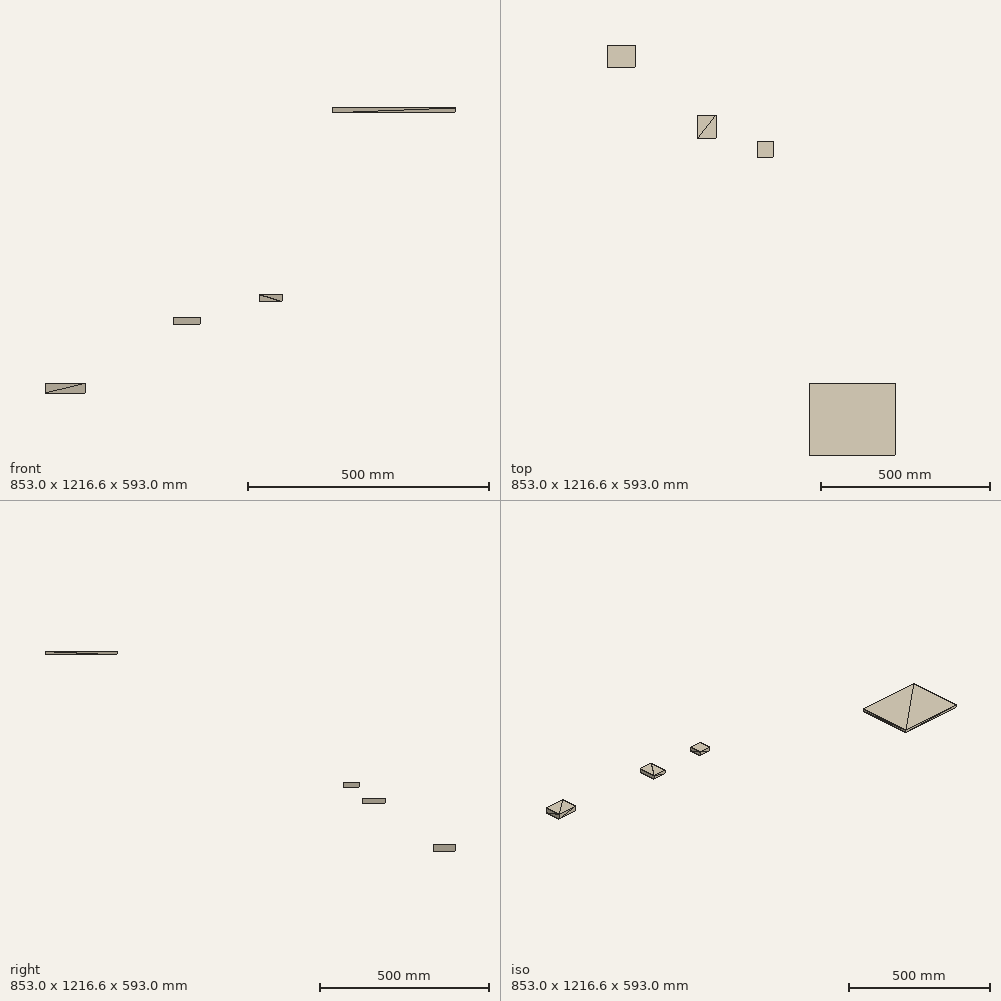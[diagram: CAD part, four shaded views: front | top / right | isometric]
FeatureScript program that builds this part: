
annotation { "Feature Type Name" : "Feature", "Feature Type Description" : "" }
export const myFeature = defineFeature(function(context is Context, id is Id, definition is map)
    precondition{}
    {
        {
            var Q0;
            Q0=qCreatedBy(makeId("Top.planeOp"),FACE);
            var sketch = newSketch(context, id + "F0", { "sketchPlane" : qUnion([Q0])});
            skLineSegment(sketch, "E0.bottom", {"start": v(-671.04, -957.1) * mm, "end": v(-416.04, -957.1) * mm});
            skLineSegment(sketch, "E0.top", {"start": v(-671.04, -1172.1) * mm, "end": v(-416.04, -1172.1) * mm});
            skLineSegment(sketch, "E0.left", {"start": v(-671.04, -957.1) * mm, "end": v(-671.04, -1172.1) * mm});
            skLineSegment(sketch, "E0.right", {"start": v(-416.04, -957.1) * mm, "end": v(-416.04, -1172.1) * mm});
            skSolve(sketch);
        }
        {
            var Q0;
            Q0=qCreatedBy(makeId("Top.planeOp"),FACE);
            var sketch = newSketch(context, id + "F1", { "sketchPlane" : qUnion([Q0])});
            skLineSegment(sketch, "E1.bottom", {"start": v(-508.52, -162.3) * mm, "end": v(-453.52, -162.3) * mm});
            skLineSegment(sketch, "E1.top", {"start": v(-508.52, -232.3) * mm, "end": v(-453.52, -232.3) * mm});
            skLineSegment(sketch, "E1.left", {"start": v(-508.52, -162.3) * mm, "end": v(-508.52, -232.3) * mm});
            skLineSegment(sketch, "E1.right", {"start": v(-453.52, -162.3) * mm, "end": v(-453.52, -232.3) * mm});
            skSolve(sketch);
        }
        {
            var Q0;
            Q0=qCreatedBy(makeId("Top.planeOp"),FACE);
            var sketch = newSketch(context, id + "F2", { "sketchPlane" : qUnion([Q0])});
            skLineSegment(sketch, "E2.bottom", {"start": v(-178.82, -239.95) * mm, "end": v(-130.82, -239.95) * mm});
            skLineSegment(sketch, "E2.top", {"start": v(-178.82, -287.95) * mm, "end": v(-130.82, -287.95) * mm});
            skLineSegment(sketch, "E2.left", {"start": v(-178.82, -239.95) * mm, "end": v(-178.82, -287.95) * mm});
            skLineSegment(sketch, "E2.right", {"start": v(-130.82, -239.95) * mm, "end": v(-130.82, -287.95) * mm});
            skSolve(sketch);
        }
        {
            var Q0;
            Q0=qCreatedBy(makeId("Top.planeOp"),FACE);
            var sketch = newSketch(context, id + "F3", { "sketchPlane" : qUnion([Q0])});
            skLineSegment(sketch, "E3.bottom", {"start": v(-665.08, 44.53) * mm, "end": v(-582.08, 44.53) * mm});
            skLineSegment(sketch, "E3.top", {"start": v(-665.08, -20.47) * mm, "end": v(-582.08, -20.47) * mm});
            skLineSegment(sketch, "E3.left", {"start": v(-665.08, 44.53) * mm, "end": v(-665.08, -20.47) * mm});
            skLineSegment(sketch, "E3.right", {"start": v(-582.08, 44.53) * mm, "end": v(-582.08, -20.47) * mm});
            skSolve(sketch);
        }
        {
            var Q0;
            Q0 = qSketchRegion(id + "F1", true);
            extrude(context, id + "F4", {"entities" : qUnion([Q0]), "depth" : 15 * mm});
        }
        {
            var Q0;
            Q0 = qSketchRegion(id + "F2", true);
            extrude(context, id + "F5", {"entities" : qUnion([Q0]), "depth" : 15 * mm});
        }
        {
            var Q0;
            Q0 = qSketchRegion(id + "F3", true);
            extrude(context, id + "F6", {"entities" : qUnion([Q0]), "depth" : 20 * mm});
        }
        {
            var Q0;
            Q0=makeQuery(id+"F0.imprint","IMPRINT",FACE,{"disambiguationData":[TD([[makeQuery(id+"F0.imprint","IMPRINT",EDGE,{"derivedFrom":sQuery(id+"F0.wireOp",EDGE,"E0.bottom")}),-1.0]])]});
            extrude(context, id + "F7", {"entities" : qUnion([Q0]), "depth" : 10 * mm});
        }
        {
            var Q0;
            Q0=makeQuery(id+"F7.opExtrude","SWEPT_BODY",BODY,{"disambiguationData":[OSD([sQuery(id+"F0.wireOp",EDGE,"E0.bottom"),sQuery(id+"F0.wireOp",EDGE,"E0.top"),sQuery(id+"F0.wireOp",EDGE,"E0.left"),sQuery(id+"F0.wireOp",EDGE,"E0.right")])]});
            transform(context, id + "F8", {"entities" : qUnion([Q0]), "transformType" : TransformType.TRANSLATION_3D, "dx" : 494 * mm, "dy" : 0 * mm, "dz" : 441 * mm, "makeCopy" : false});
        }
        {
            var Q0;
            Q0=makeQuery(id+"F5.opExtrude","SWEPT_BODY",BODY,{"disambiguationData":[OSD([sQuery(id+"F2.wireOp",EDGE,"E2.bottom"),sQuery(id+"F2.wireOp",EDGE,"E2.top"),sQuery(id+"F2.wireOp",EDGE,"E2.left"),sQuery(id+"F2.wireOp",EDGE,"E2.right")])]});
            transform(context, id + "F9", {"entities" : qUnion([Q0]), "transformType" : TransformType.TRANSLATION_3D, "dx" : -152 * mm, "dy" : 0 * mm, "dz" : 48 * mm, "makeCopy" : false});
        }
        {
            var Q0;
            Q0=makeQuery(id+"F6.opExtrude","SWEPT_BODY",BODY,{"disambiguationData":[OSD([sQuery(id+"F3.wireOp",EDGE,"E3.bottom"),sQuery(id+"F3.wireOp",EDGE,"E3.top"),sQuery(id+"F3.wireOp",EDGE,"E3.left"),sQuery(id+"F3.wireOp",EDGE,"E3.right")])]});
            transform(context, id + "F10", {"entities" : qUnion([Q0]), "transformType" : TransformType.TRANSLATION_3D, "dx" : -110 * mm, "dy" : 0 * mm, "dz" : -142 * mm, "makeCopy" : false});
        }
    });
